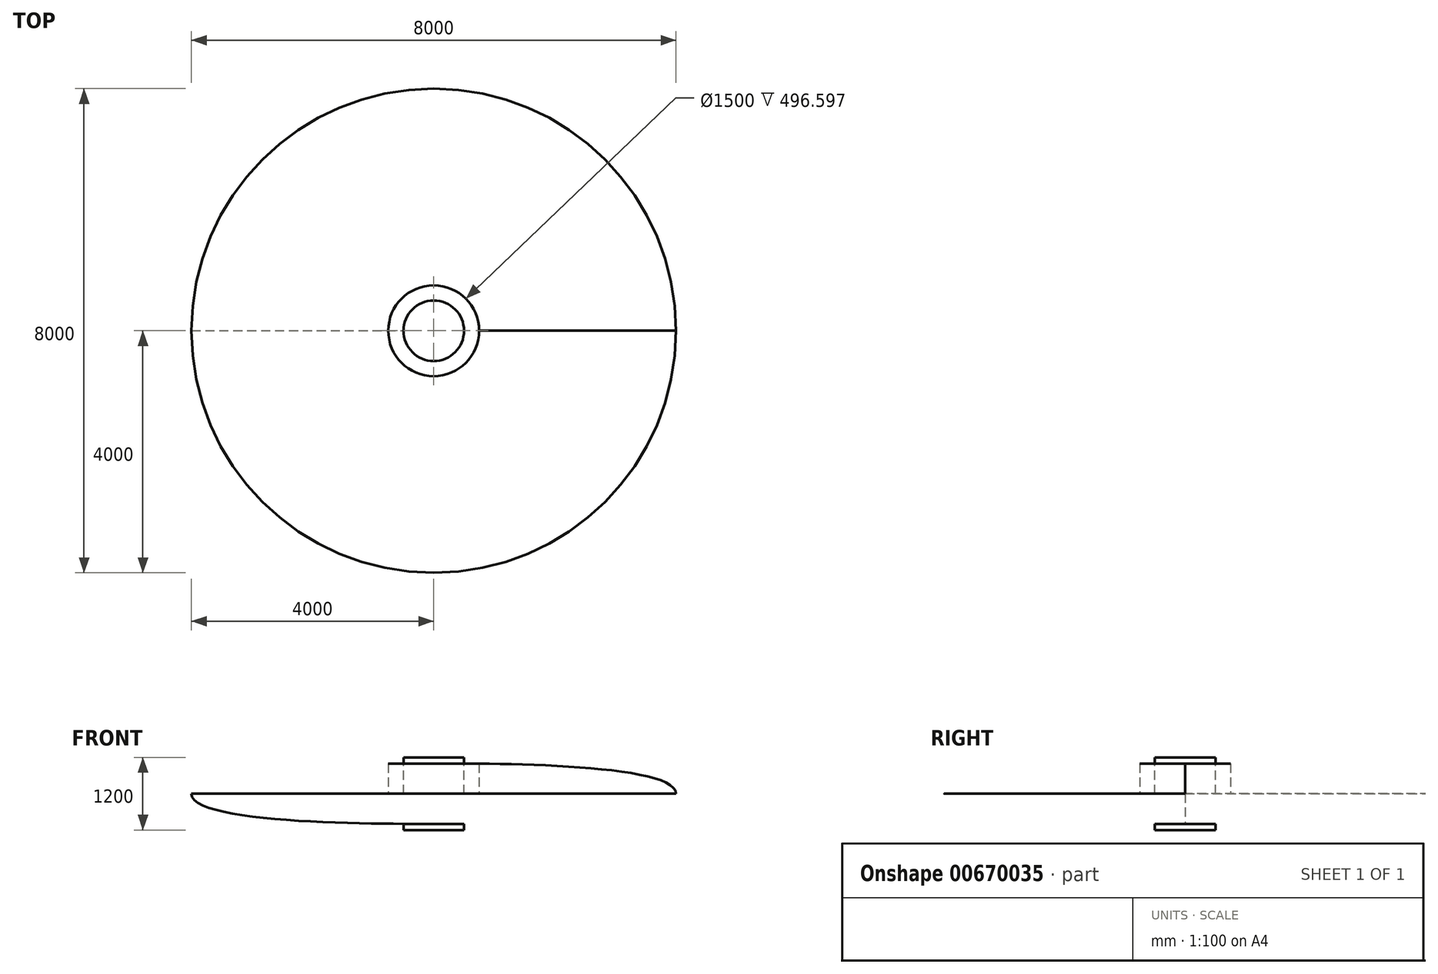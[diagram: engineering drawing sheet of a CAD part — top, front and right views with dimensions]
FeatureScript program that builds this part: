
annotation { "Feature Type Name" : "Feature", "Feature Type Description" : "" }
export const myFeature = defineFeature(function(context is Context, id is Id, definition is map)
    precondition{}
    {
        {
            var Q0;
            Q0=qCreatedBy(makeId("Front.planeOp"),FACE);
            var sketch = newSketch(context, id + "F0", { "sketchPlane" : qUnion([Q0])});
            skFitSpline(sketch, "E0", {"points": [v(-4000, 0) * mm, v(0, 500) * mm], "startDerivative": vector(0, 1500) * mm, "endDerivative": vector(3000, 0) * mm});
            skLineSegment(sketch, "E1", {"start": v(0, 0) * mm, "end": v(-4000, 0) * mm});
            skLineSegment(sketch, "E2", {"start": v(0, 500) * mm, "end": v(0, 0) * mm});
            skSolve(sketch);
        }
        {
            var Q0;
            Q0=makeQuery(id+"F0.imprint","IMPRINT",FACE,{"disambiguationData":[TD([[makeQuery(id+"F0.imprint","IMPRINT",EDGE,{"derivedFrom":sQuery(id+"F0.wireOp",EDGE,"E0")}),-1.0]])]});
            var Q1;
            Q1=sQuery(id+"F0.wireOp",EDGE,"E2");
            revolve(context, id + "F1", {"entities" : qUnion([Q0]), "axis" : qUnion([Q1]), "revolveType" : RevolveType.FULL});
        }
        {
            var Q0;
            Q0=makeQuery(id+"F1.opRevolve","SWEPT_BODY",BODY,{"disambiguationData":[OSD([sQuery(id+"F0.wireOp",EDGE,"E0"),sQuery(id+"F0.wireOp",EDGE,"E1"),sQuery(id+"F0.wireOp",EDGE,"E2")])]});
            var Q1;
            Q1=qCreatedBy(makeId("Top.planeOp"),FACE);
            mirror(context, id + "F2", {"operationType" : NewBodyOperationType.ADD, "entities" : qUnion([Q0]), "mirrorPlane" : qUnion([Q1])});
        }
        {
            var Q0;
            Q0=qCreatedBy(makeId("Front.planeOp"),FACE);
            var sketch = newSketch(context, id + "F3", { "sketchPlane" : qUnion([Q0])});
            skLineSegment(sketch, "E3.bottom", {"start": v(0, 0) * mm, "end": v(-750, 0) * mm});
            skLineSegment(sketch, "E3.top", {"start": v(0, 500) * mm, "end": v(-750, 500) * mm});
            skLineSegment(sketch, "E3.left", {"start": v(0, 0) * mm, "end": v(0, 500) * mm});
            skLineSegment(sketch, "E3.right", {"start": v(-750, 0) * mm, "end": v(-750, 500) * mm});
            skLineSegment(sketch, "E4.left", {"start": v(-750, 500) * mm, "end": v(-750, 500) * mm});
            skLineSegment(sketch, "E4.right", {"start": v(-1115.8, 500) * mm, "end": v(-1115.8, 500) * mm});
            skSolve(sketch);
        }
        {
            var Q0;
            Q0 = qSketchRegion(id + "F3", true);
            var Q1;
            Q1=sQuery(id+"F0.wireOp",EDGE,"E2");
            revolve(context, id + "F4", {"operationType" : NewBodyOperationType.REMOVE, "entities" : qUnion([Q0]), "axis" : qUnion([Q1]), "revolveType" : RevolveType.FULL, "oppositeDirection" : true});
        }
        {
            var Q0;
            Q0=qCreatedBy(makeId("Front.planeOp"),FACE);
            var sketch = newSketch(context, id + "F5", { "sketchPlane" : qUnion([Q0])});
            skLineSegment(sketch, "E5.bottom", {"start": v(0, 0) * mm, "end": v(500, 0) * mm});
            skLineSegment(sketch, "E5.top", {"start": v(0, 600) * mm, "end": v(500, 600) * mm});
            skLineSegment(sketch, "E5.left", {"start": v(0, 0) * mm, "end": v(0, 600) * mm});
            skLineSegment(sketch, "E5.right", {"start": v(500, 0) * mm, "end": v(500, 600) * mm});
            skSolve(sketch);
        }
        {
            var Q0;
            Q0 = qSketchRegion(id + "F5", true);
            var Q1;
            Q1=sQuery(id+"F0.wireOp",EDGE,"E2");
            revolve(context, id + "F6", {"entities" : qUnion([Q0]), "axis" : qUnion([Q1]), "revolveType" : RevolveType.FULL});
        }
        {
            var Q0;
            Q0=makeQuery(id+"F6.opRevolve","SWEPT_BODY",BODY,{"disambiguationData":[OSD([sQuery(id+"F5.wireOp",EDGE,"E5.bottom"),sQuery(id+"F5.wireOp",EDGE,"E5.top"),sQuery(id+"F5.wireOp",EDGE,"E5.left"),sQuery(id+"F5.wireOp",EDGE,"E5.right")])]});
            var Q1;
            Q1=qCreatedBy(makeId("Top.planeOp"),FACE);
            mirror(context, id + "F7", {"operationType" : NewBodyOperationType.ADD, "entities" : qUnion([Q0]), "mirrorPlane" : qUnion([Q1])});
        }
    });
